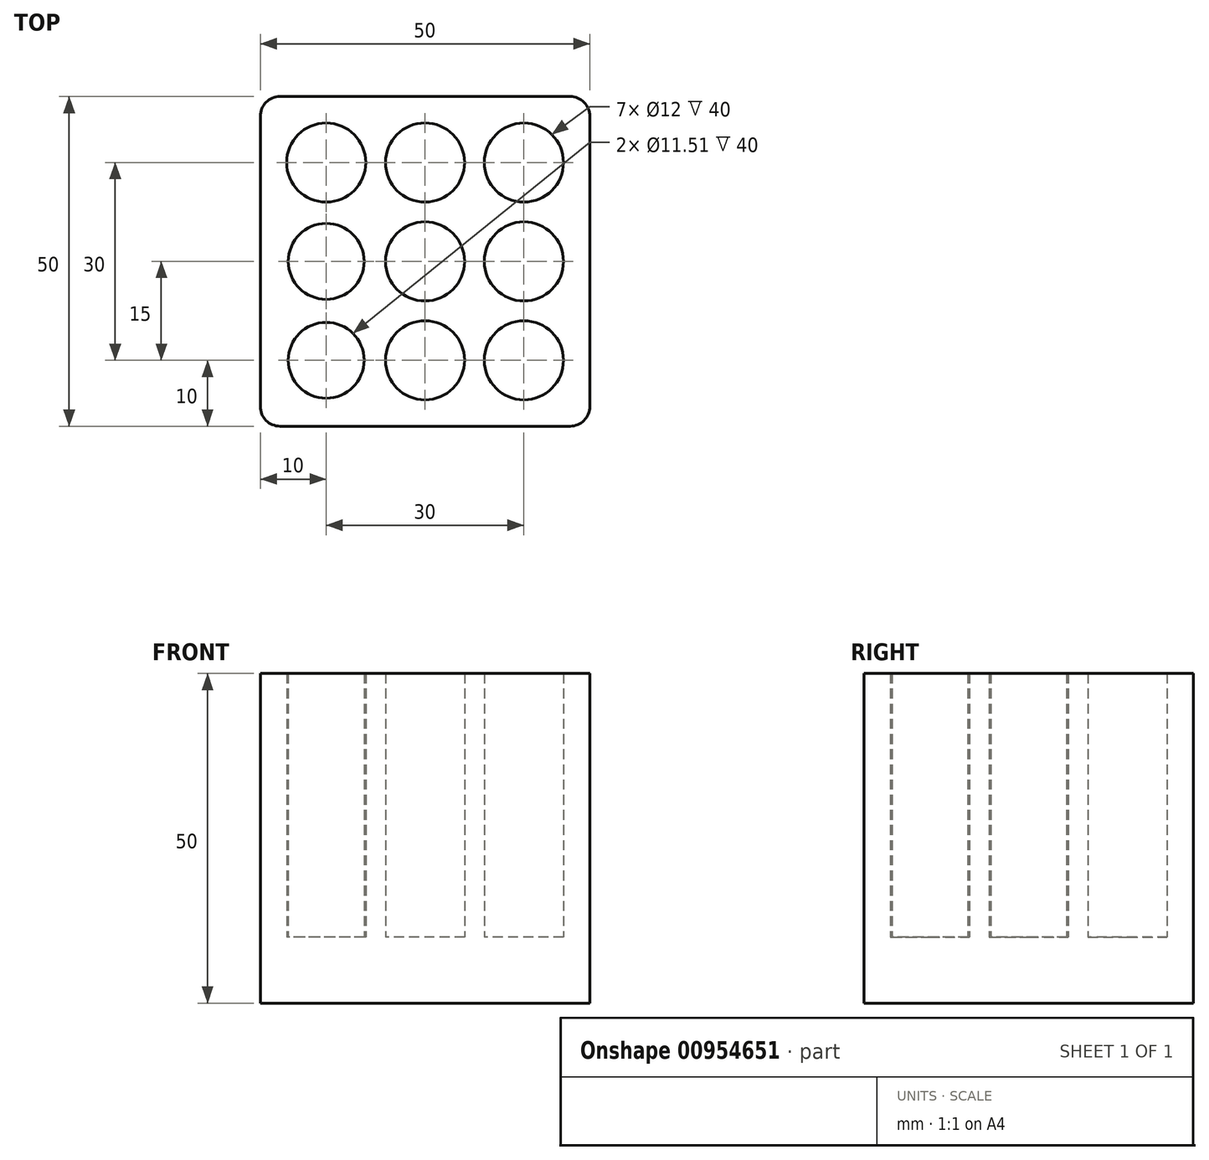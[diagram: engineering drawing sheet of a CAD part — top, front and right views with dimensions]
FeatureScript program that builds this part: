
annotation { "Feature Type Name" : "Feature", "Feature Type Description" : "" }
export const myFeature = defineFeature(function(context is Context, id is Id, definition is map)
    precondition{}
    {
        {
            var Q0;
            Q0=qCreatedBy(makeId("Top.planeOp"),FACE);
            var sketch = newSketch(context, id + "F0", { "sketchPlane" : qUnion([Q0])});
            skCircle(sketch, "E0", {"center": v(0, 0) * mm, "radius": 6 * mm});
            skCircle(sketch, "E1", {"center": v(0, 15) * mm, "radius": 6 * mm});
            skCircle(sketch, "E2", {"center": v(-15, 0) * mm, "radius": 5.75 * mm});
            skCircle(sketch, "E3", {"center": v(15, 0) * mm, "radius": 6 * mm});
            skCircle(sketch, "E4", {"center": v(0, -15) * mm, "radius": 6 * mm});
            skCircle(sketch, "E5", {"center": v(-15, 15) * mm, "radius": 6 * mm});
            skCircle(sketch, "E6", {"center": v(15, 15) * mm, "radius": 6 * mm});
            skCircle(sketch, "E7", {"center": v(15, -15) * mm, "radius": 6 * mm});
            skCircle(sketch, "E8", {"center": v(-15, -15) * mm, "radius": 5.75 * mm});
            skLineSegment(sketch, "E9.bottom", {"start": v(22, 25) * mm, "end": v(-22, 25) * mm});
            skLineSegment(sketch, "E9.top", {"start": v(22, -25) * mm, "end": v(-22, -25) * mm});
            skLineSegment(sketch, "E9.left", {"start": v(25, 22) * mm, "end": v(25, -22) * mm});
            skLineSegment(sketch, "E9.right", {"start": v(-25, 22) * mm, "end": v(-25, -22) * mm});
            skPoint(sketch, "E10.visualSharp", {"position": v(25, 25) * mm});
            skArc(sketch, "E10.filletArc", {"start": v(25, 22) * mm, "mid": v(24.12, 24.12) * mm, "end": v(22, 25) * mm});
            skPoint(sketch, "E11.visualSharp", {"position": v(-25, 25) * mm});
            skArc(sketch, "E11.filletArc", {"start": v(-22, 25) * mm, "mid": v(-24.12, 24.12) * mm, "end": v(-25, 22) * mm});
            skPoint(sketch, "E12.visualSharp", {"position": v(-25, -25) * mm});
            skArc(sketch, "E12.filletArc", {"start": v(-25, -22) * mm, "mid": v(-24.12, -24.12) * mm, "end": v(-22, -25) * mm});
            skPoint(sketch, "E13.visualSharp", {"position": v(25, -25) * mm});
            skArc(sketch, "E13.filletArc", {"start": v(22, -25) * mm, "mid": v(24.12, -24.12) * mm, "end": v(25, -22) * mm});
            skSolve(sketch);
        }
        {
            var Q0;
            Q0 = qSketchRegion(id + "F0", true);
            extrude(context, id + "F1", {"entities" : qUnion([Q0]), "depth" : 40 * mm, "offsetDistance" : 25 * mm});
        }
        {
            var Q0;
            Q0=makeQuery(id+"F1.opExtrude","CAP_FACE",FACE,{"disambiguationData":[OSD([sQuery(id+"F0.wireOp",EDGE,"E0"),sQuery(id+"F0.wireOp",EDGE,"E1"),sQuery(id+"F0.wireOp",EDGE,"E2"),sQuery(id+"F0.wireOp",EDGE,"E3"),sQuery(id+"F0.wireOp",EDGE,"E4"),sQuery(id+"F0.wireOp",EDGE,"E5"),sQuery(id+"F0.wireOp",EDGE,"E6"),sQuery(id+"F0.wireOp",EDGE,"E7"),sQuery(id+"F0.wireOp",EDGE,"E8"),sQuery(id+"F0.wireOp",EDGE,"E9.bottom"),sQuery(id+"F0.wireOp",EDGE,"E9.top"),sQuery(id+"F0.wireOp",EDGE,"E9.left"),sQuery(id+"F0.wireOp",EDGE,"E9.right"),sQuery(id+"F0.wireOp",EDGE,"E10.filletArc"),sQuery(id+"F0.wireOp",EDGE,"E11.filletArc"),sQuery(id+"F0.wireOp",EDGE,"E12.filletArc"),sQuery(id+"F0.wireOp",EDGE,"E13.filletArc")])],"isStart":true});
            var sketch = newSketch(context, id + "F2", { "sketchPlane" : qUnion([Q0])});
            skLineSegment(sketch, "E14.bottom", {"start": v(22, 25) * mm, "end": v(-22, 25) * mm});
            skLineSegment(sketch, "E14.top", {"start": v(22, -25) * mm, "end": v(-22, -25) * mm});
            skLineSegment(sketch, "E14.left", {"start": v(25, 22) * mm, "end": v(25, -22) * mm});
            skLineSegment(sketch, "E14.right", {"start": v(-25, 22) * mm, "end": v(-25, -22) * mm});
            skPoint(sketch, "E14.middle", {"position": v(0, 0) * mm});
            skPoint(sketch, "E15.visualSharp", {"position": v(-25, 25) * mm});
            skArc(sketch, "E15.filletArc", {"start": v(-22, 25) * mm, "mid": v(-24.12, 24.12) * mm, "end": v(-25, 22) * mm});
            skPoint(sketch, "E16.visualSharp", {"position": v(25, 25) * mm});
            skArc(sketch, "E16.filletArc", {"start": v(25, 22) * mm, "mid": v(24.12, 24.12) * mm, "end": v(22, 25) * mm});
            skPoint(sketch, "E17.visualSharp", {"position": v(25, -25) * mm});
            skArc(sketch, "E17.filletArc", {"start": v(22, -25) * mm, "mid": v(24.12, -24.12) * mm, "end": v(25, -22) * mm});
            skPoint(sketch, "E18.visualSharp", {"position": v(-25, -25) * mm});
            skArc(sketch, "E18.filletArc", {"start": v(-25, -22) * mm, "mid": v(-24.12, -24.12) * mm, "end": v(-22, -25) * mm});
            skSolve(sketch);
        }
        {
            var Q0;
            Q0 = qSketchRegion(id + "F2", true);
            extrude(context, id + "F3", {"entities" : qUnion([Q0]), "operationType" : NewBodyOperationType.ADD, "depth" : 10 * mm, "offsetDistance" : 25 * mm});
        }
    });
